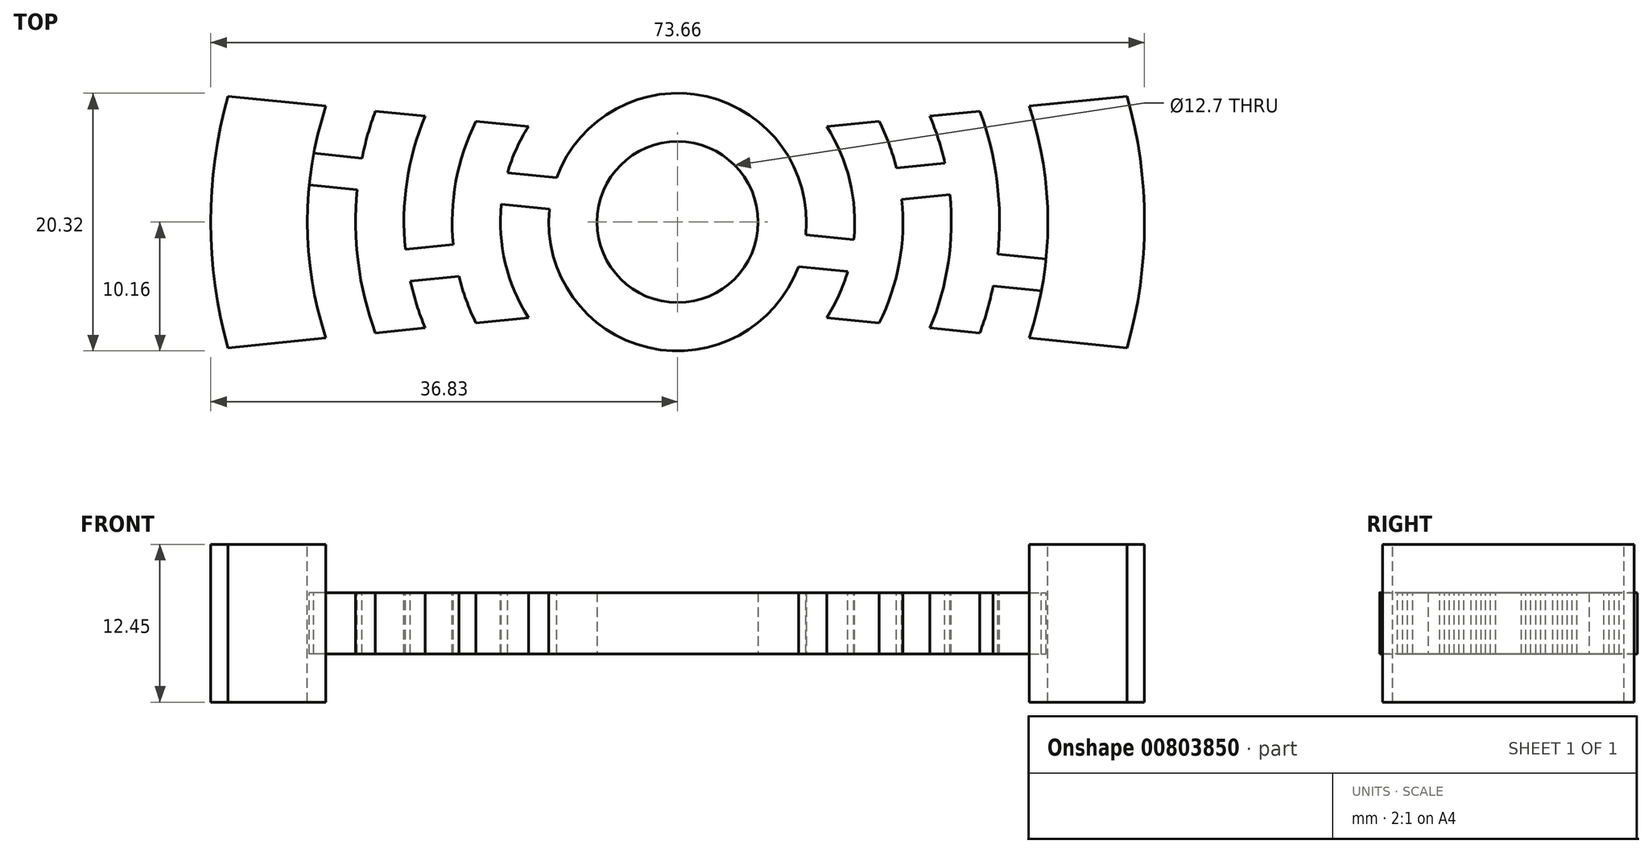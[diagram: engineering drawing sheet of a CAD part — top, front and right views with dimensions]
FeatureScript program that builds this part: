
annotation { "Feature Type Name" : "Feature", "Feature Type Description" : "" }
export const myFeature = defineFeature(function(context is Context, id is Id, definition is map)
    precondition{}
    {
        {
            var Q0;
            Q0=qCreatedBy(makeId("Top.planeOp"),FACE);
            var sketch = newSketch(context, id + "F0", { "sketchPlane" : qUnion([Q0])});
            skCircle(sketch, "E0", {"center": v(0, 0) * mm, "radius": 6.35 * mm});
            skCircle(sketch, "E1", {"center": v(0, 0) * mm, "radius": 10.16 * mm});
            skLineSegment(sketch, "E2", {"start": v(0, 6.35) * mm, "end": v(-37.9, 10.16) * mm});
            skLineSegment(sketch, "E3", {"start": v(0, -6.35) * mm, "end": v(-37.9, -10.16) * mm});
            skLineSegment(sketch, "E4", {"start": v(0, 6.35) * mm, "end": v(37.9, 10.16) * mm});
            skLineSegment(sketch, "E5", {"start": v(0, -6.35) * mm, "end": v(37.9, -10.16) * mm});
            skLineSegment(sketch, "E6", {"start": v(0, 0) * mm, "end": v(40.64, 0) * mm});
            skLineSegment(sketch, "E7", {"start": v(0, 0) * mm, "end": v(-40.64, 0) * mm});
            skCircle(sketch, "E8", {"center": v(0, 0) * mm, "radius": 39.25 * mm});
            skSolve(sketch);
        }
        {
            var Q0;
            {var subQ0=sQuery(id+"F0.wireOp",EDGE,"E4");var subQ1=sQuery(id+"F0.wireOp",EDGE,"E1");var subQ2=makeQuery(id+"F0.imprint","INTERSECT",VERTEX,{"derivedFrom":[subQ1,subQ0]});Q0=makeQuery(id+"F0.imprint","IMPRINT",FACE,{"disambiguationData":[TD([[makeQuery(id+"F0.imprint","IMPRINT",EDGE,{"disambiguationData":[TD([[subQ2,1.0]])],"derivedFrom":subQ1}),-1.0]])]});}
            var Q1;
            {var subQ0=sQuery(id+"F0.wireOp",EDGE,"E2");var subQ1=sQuery(id+"F0.wireOp",EDGE,"E1");var subQ2=makeQuery(id+"F0.imprint","INTERSECT",VERTEX,{"derivedFrom":[subQ1,subQ0]});Q1=makeQuery(id+"F0.imprint","IMPRINT",FACE,{"disambiguationData":[TD([[makeQuery(id+"F0.imprint","IMPRINT",EDGE,{"disambiguationData":[TD([[subQ2,-1.0]])],"derivedFrom":subQ1}),-1.0]])]});}
            var Q2;
            {var subQ0=sQuery(id+"F0.wireOp",EDGE,"E7");var subQ1=sQuery(id+"F0.wireOp",EDGE,"E1");var subQ2=makeQuery(id+"F0.imprint","INTERSECT",VERTEX,{"derivedFrom":[subQ1,subQ0]});Q2=makeQuery(id+"F0.imprint","IMPRINT",FACE,{"disambiguationData":[TD([[makeQuery(id+"F0.imprint","IMPRINT",EDGE,{"disambiguationData":[TD([[subQ2,-1.0]])],"derivedFrom":subQ1}),-1.0]])]});}
            var Q3;
            {var subQ0=sQuery(id+"F0.wireOp",EDGE,"E6");var subQ1=sQuery(id+"F0.wireOp",EDGE,"E1");var subQ2=makeQuery(id+"F0.imprint","INTERSECT",VERTEX,{"derivedFrom":[subQ1,subQ0]});Q3=makeQuery(id+"F0.imprint","IMPRINT",FACE,{"disambiguationData":[TD([[makeQuery(id+"F0.imprint","IMPRINT",EDGE,{"disambiguationData":[TD([[subQ2,1.0]])],"derivedFrom":subQ1}),-1.0]])]});}
            var Q4;
            {var subQ0=sQuery(id+"F0.wireOp",EDGE,"E2");var subQ5=sQuery(id+"F0.wireOp",EDGE,"E1");var subQ6=makeQuery(id+"F0.imprint","INTERSECT",VERTEX,{"derivedFrom":[subQ5,subQ0]});Q4=makeQuery(id+"F0.imprint","IMPRINT",FACE,{"disambiguationData":[TD([[makeQuery(id+"F0.imprint","IMPRINT",EDGE,{"disambiguationData":[TD([[subQ6,-1.0]])],"derivedFrom":subQ5}),1.0]])]});}
            var Q5;
            {var subQ3=sQuery(id+"F0.wireOp",EDGE,"E7");var subQ5=sQuery(id+"F0.wireOp",EDGE,"E1");var subQ6=makeQuery(id+"F0.imprint","INTERSECT",VERTEX,{"derivedFrom":[subQ5,subQ3]});Q5=makeQuery(id+"F0.imprint","IMPRINT",FACE,{"disambiguationData":[TD([[makeQuery(id+"F0.imprint","IMPRINT",EDGE,{"disambiguationData":[TD([[subQ6,-1.0]])],"derivedFrom":subQ5}),1.0]])]});}
            var Q6;
            {var subQ3=sQuery(id+"F0.wireOp",EDGE,"E6");var subQ5=sQuery(id+"F0.wireOp",EDGE,"E1");var subQ6=makeQuery(id+"F0.imprint","INTERSECT",VERTEX,{"derivedFrom":[subQ5,subQ3]});Q6=makeQuery(id+"F0.imprint","IMPRINT",FACE,{"disambiguationData":[TD([[makeQuery(id+"F0.imprint","IMPRINT",EDGE,{"disambiguationData":[TD([[subQ6,1.0]])],"derivedFrom":subQ5}),1.0]])]});}
            var Q7;
            {var subQ0=sQuery(id+"F0.wireOp",EDGE,"E4");var subQ5=sQuery(id+"F0.wireOp",EDGE,"E1");var subQ6=makeQuery(id+"F0.imprint","INTERSECT",VERTEX,{"derivedFrom":[subQ5,subQ0]});Q7=makeQuery(id+"F0.imprint","IMPRINT",FACE,{"disambiguationData":[TD([[makeQuery(id+"F0.imprint","IMPRINT",EDGE,{"disambiguationData":[TD([[subQ6,1.0]])],"derivedFrom":subQ5}),1.0]])]});}
            var Q8;
            {var subQ0=sQuery(id+"F0.wireOp",EDGE,"E4");var subQ1=sQuery(id+"F0.wireOp",EDGE,"E1");var subQ2=makeQuery(id+"F0.imprint","INTERSECT",VERTEX,{"derivedFrom":[subQ1,subQ0]});Q8=makeQuery(id+"F0.imprint","IMPRINT",FACE,{"disambiguationData":[TD([[makeQuery(id+"F0.imprint","IMPRINT",EDGE,{"disambiguationData":[TD([[subQ2,-1.0]])],"derivedFrom":subQ1}),1.0]])]});}
            var Q9;
            {var subQ0=sQuery(id+"F0.wireOp",EDGE,"E3");var subQ1=sQuery(id+"F0.wireOp",EDGE,"E1");var subQ2=makeQuery(id+"F0.imprint","INTERSECT",VERTEX,{"derivedFrom":[subQ1,subQ0]});Q9=makeQuery(id+"F0.imprint","IMPRINT",FACE,{"disambiguationData":[TD([[makeQuery(id+"F0.imprint","IMPRINT",EDGE,{"disambiguationData":[TD([[subQ2,-1.0]])],"derivedFrom":subQ1}),1.0]])]});}
            extrude(context, id + "F1", {"entities" : qUnion([Q0, Q1, Q2, Q3, Q4, Q5, Q6, Q7, Q8, Q9]), "depth" : 4.83 * mm, "offsetDistance" : 25.4 * mm});
        }
        {
            var Q0;
            Q0=makeQuery(id+"F1.opExtrude","CAP_FACE",FACE,{"disambiguationData":[OSD([sQuery(id+"F0.wireOp",EDGE,"E0"),sQuery(id+"F0.wireOp",EDGE,"E1"),sQuery(id+"F0.wireOp",EDGE,"E2"),sQuery(id+"F0.wireOp",EDGE,"E3"),sQuery(id+"F0.wireOp",EDGE,"E4"),sQuery(id+"F0.wireOp",EDGE,"E5"),sQuery(id+"F0.wireOp",EDGE,"liuHo2mv-Kwf8-5aol-AB9t-589r57ZSycez"),sQuery(id+"F0.wireOp",EDGE,"nakFOlJR-s7SA-ednX-MnhK-JYGa1BLhNWg9")])],"isStart":false});
            var sketch = newSketch(context, id + "F2", { "sketchPlane" : qUnion([Q0])});
            skCircle(sketch, "E9", {"center": v(0, 0) * mm, "radius": 6.35 * mm});
            skCircle(sketch, "E10", {"center": v(0, 0) * mm, "radius": 10.16 * mm});
            skCircle(sketch, "E11", {"center": v(0, 0) * mm, "radius": 39.25 * mm});
            skCircle(sketch, "E12", {"center": v(0, 0) * mm, "radius": 33.02 * mm});
            skCircle(sketch, "E13", {"center": v(0, 0) * mm, "radius": 25.4 * mm});
            skCircle(sketch, "E14", {"center": v(0, 0) * mm, "radius": 21.59 * mm});
            skCircle(sketch, "E15", {"center": v(0, 0) * mm, "radius": 29.21 * mm});
            skCircle(sketch, "E16", {"center": v(0, 0) * mm, "radius": 13.97 * mm});
            skCircle(sketch, "E17", {"center": v(0, 0) * mm, "radius": 17.78 * mm});
            skCircle(sketch, "E18", {"center": v(0, 0) * mm, "radius": 2.54 * mm});
            skLineSegment(sketch, "E19", {"start": v(0, -2.54) * mm, "end": v(-38.72, -6.43) * mm});
            skLineSegment(sketch, "E20", {"start": v(0, 2.54) * mm, "end": v(-38.72, 6.43) * mm});
            skLineSegment(sketch, "E21", {"start": v(0, -2.54) * mm, "end": v(38.72, -6.43) * mm});
            skLineSegment(sketch, "E22", {"start": v(0, 2.54) * mm, "end": v(38.72, 6.43) * mm});
            skLineSegment(sketch, "E23", {"start": v(0, 0) * mm, "end": v(-39.05, 3.92) * mm});
            skLineSegment(sketch, "E24", {"start": v(0, 0) * mm, "end": v(39.05, 3.92) * mm});
            skLineSegment(sketch, "E25", {"start": v(0, 0) * mm, "end": v(39.05, -3.92) * mm});
            skLineSegment(sketch, "E26", {"start": v(0, 0) * mm, "end": v(-39.05, -3.92) * mm});
            skCircle(sketch, "E27", {"center": v(0, 0) * mm, "radius": 36.83 * mm});
            skCircle(sketch, "E28", {"center": v(0.53, -0.92) * mm, "radius": 41.7 * mm});
            skSolve(sketch);
        }
        {
            var Q0;
            {var subQ0=sQuery(id+"F2.wireOp",EDGE,"E20");var subQ1=sQuery(id+"F2.wireOp",EDGE,"E14");var subQ2=makeQuery(id+"F2.imprint","INTERSECT",VERTEX,{"derivedFrom":[subQ1,subQ0]});Q0=makeQuery(id+"F2.imprint","IMPRINT",FACE,{"disambiguationData":[TD([[makeQuery(id+"F2.imprint","IMPRINT",EDGE,{"disambiguationData":[TD([[subQ2,1.0]])],"derivedFrom":subQ1}),1.0]])]});}
            var Q1;
            {var subQ0=sQuery(id+"F2.wireOp",EDGE,"E20");var subQ1=sQuery(id+"F2.wireOp",EDGE,"E14");var subQ2=makeQuery(id+"F2.imprint","INTERSECT",VERTEX,{"derivedFrom":[subQ1,subQ0]});Q1=makeQuery(id+"F2.imprint","IMPRINT",FACE,{"disambiguationData":[TD([[makeQuery(id+"F2.imprint","IMPRINT",EDGE,{"disambiguationData":[TD([[subQ2,-1.0]])],"derivedFrom":subQ1}),1.0]])]});}
            var Q2;
            {var subQ0=sQuery(id+"F2.wireOp",EDGE,"E21");var subQ1=sQuery(id+"F2.wireOp",EDGE,"E14");var subQ2=makeQuery(id+"F2.imprint","INTERSECT",VERTEX,{"derivedFrom":[subQ1,subQ0]});Q2=makeQuery(id+"F2.imprint","IMPRINT",FACE,{"disambiguationData":[TD([[makeQuery(id+"F2.imprint","IMPRINT",EDGE,{"disambiguationData":[TD([[subQ2,1.0]])],"derivedFrom":subQ1}),1.0]])]});}
            var Q3;
            {var subQ0=sQuery(id+"F2.wireOp",EDGE,"E19");var subQ1=sQuery(id+"F2.wireOp",EDGE,"E14");var subQ2=makeQuery(id+"F2.imprint","INTERSECT",VERTEX,{"derivedFrom":[subQ1,subQ0]});Q3=makeQuery(id+"F2.imprint","IMPRINT",FACE,{"disambiguationData":[TD([[makeQuery(id+"F2.imprint","IMPRINT",EDGE,{"disambiguationData":[TD([[subQ2,-1.0]])],"derivedFrom":subQ1}),1.0]])]});}
            var Q4;
            {var subQ0=sQuery(id+"F2.wireOp",EDGE,"E19");var subQ1=sQuery(id+"F2.wireOp",EDGE,"E13");var subQ2=makeQuery(id+"F2.imprint","INTERSECT",VERTEX,{"derivedFrom":[subQ1,subQ0]});Q4=makeQuery(id+"F2.imprint","IMPRINT",FACE,{"disambiguationData":[TD([[makeQuery(id+"F2.imprint","IMPRINT",EDGE,{"disambiguationData":[TD([[subQ2,-1.0]])],"derivedFrom":subQ1}),-1.0]])]});}
            var Q5;
            {var subQ0=sQuery(id+"F2.wireOp",EDGE,"E23");var subQ1=sQuery(id+"F2.wireOp",EDGE,"E13");var subQ2=makeQuery(id+"F2.imprint","INTERSECT",VERTEX,{"derivedFrom":[subQ1,subQ0]});Q5=makeQuery(id+"F2.imprint","IMPRINT",FACE,{"disambiguationData":[TD([[makeQuery(id+"F2.imprint","IMPRINT",EDGE,{"disambiguationData":[TD([[subQ2,-1.0]])],"derivedFrom":subQ1}),-1.0]])]});}
            var Q6;
            {var subQ0=sQuery(id+"F2.wireOp",EDGE,"E20");var subQ1=sQuery(id+"F2.wireOp",EDGE,"E13");var subQ2=makeQuery(id+"F2.imprint","INTERSECT",VERTEX,{"derivedFrom":[subQ1,subQ0]});Q6=makeQuery(id+"F2.imprint","IMPRINT",FACE,{"disambiguationData":[TD([[makeQuery(id+"F2.imprint","IMPRINT",EDGE,{"disambiguationData":[TD([[subQ2,1.0]])],"derivedFrom":subQ1}),-1.0]])]});}
            var Q7;
            {var subQ0=sQuery(id+"F2.wireOp",EDGE,"E24");var subQ1=sQuery(id+"F2.wireOp",EDGE,"E14");var subQ2=makeQuery(id+"F2.imprint","INTERSECT",VERTEX,{"derivedFrom":[subQ1,subQ0]});Q7=makeQuery(id+"F2.imprint","IMPRINT",FACE,{"disambiguationData":[TD([[makeQuery(id+"F2.imprint","IMPRINT",EDGE,{"disambiguationData":[TD([[subQ2,1.0]])],"derivedFrom":subQ1}),1.0]])]});}
            var Q8;
            {var subQ0=sQuery(id+"F2.wireOp",EDGE,"E21");var subQ1=sQuery(id+"F2.wireOp",EDGE,"E14");var subQ2=makeQuery(id+"F2.imprint","INTERSECT",VERTEX,{"derivedFrom":[subQ1,subQ0]});Q8=makeQuery(id+"F2.imprint","IMPRINT",FACE,{"disambiguationData":[TD([[makeQuery(id+"F2.imprint","IMPRINT",EDGE,{"disambiguationData":[TD([[subQ2,-1.0]])],"derivedFrom":subQ1}),1.0]])]});}
            var Q9;
            {var subQ0=sQuery(id+"F2.wireOp",EDGE,"E22");var subQ1=sQuery(id+"F2.wireOp",EDGE,"E14");var subQ2=makeQuery(id+"F2.imprint","INTERSECT",VERTEX,{"derivedFrom":[subQ1,subQ0]});Q9=makeQuery(id+"F2.imprint","IMPRINT",FACE,{"disambiguationData":[TD([[makeQuery(id+"F2.imprint","IMPRINT",EDGE,{"disambiguationData":[TD([[subQ2,-1.0]])],"derivedFrom":subQ1}),1.0]])]});}
            var Q10;
            {var subQ0=sQuery(id+"F2.wireOp",EDGE,"E22");var subQ1=sQuery(id+"F2.wireOp",EDGE,"E13");var subQ2=makeQuery(id+"F2.imprint","INTERSECT",VERTEX,{"derivedFrom":[subQ1,subQ0]});Q10=makeQuery(id+"F2.imprint","IMPRINT",FACE,{"disambiguationData":[TD([[makeQuery(id+"F2.imprint","IMPRINT",EDGE,{"disambiguationData":[TD([[subQ2,-1.0]])],"derivedFrom":subQ1}),-1.0]])]});}
            var Q11;
            {var subQ0=sQuery(id+"F2.wireOp",EDGE,"E22");var subQ1=sQuery(id+"F2.wireOp",EDGE,"E13");var subQ2=makeQuery(id+"F2.imprint","INTERSECT",VERTEX,{"derivedFrom":[subQ1,subQ0]});Q11=makeQuery(id+"F2.imprint","IMPRINT",FACE,{"disambiguationData":[TD([[makeQuery(id+"F2.imprint","IMPRINT",EDGE,{"disambiguationData":[TD([[subQ2,1.0]])],"derivedFrom":subQ1}),-1.0]])]});}
            var Q12;
            {var subQ0=sQuery(id+"F2.wireOp",EDGE,"E24");var subQ1=sQuery(id+"F2.wireOp",EDGE,"E13");var subQ2=makeQuery(id+"F2.imprint","INTERSECT",VERTEX,{"derivedFrom":[subQ1,subQ0]});Q12=makeQuery(id+"F2.imprint","IMPRINT",FACE,{"disambiguationData":[TD([[makeQuery(id+"F2.imprint","IMPRINT",EDGE,{"disambiguationData":[TD([[subQ2,1.0]])],"derivedFrom":subQ1}),-1.0]])]});}
            var Q13;
            {var subQ0=sQuery(id+"F2.wireOp",EDGE,"E21");var subQ1=sQuery(id+"F2.wireOp",EDGE,"E13");var subQ2=makeQuery(id+"F2.imprint","INTERSECT",VERTEX,{"derivedFrom":[subQ1,subQ0]});Q13=makeQuery(id+"F2.imprint","IMPRINT",FACE,{"disambiguationData":[TD([[makeQuery(id+"F2.imprint","IMPRINT",EDGE,{"disambiguationData":[TD([[subQ2,1.0]])],"derivedFrom":subQ1}),-1.0]])]});}
            var Q14;
            {var subQ0=sQuery(id+"F2.wireOp",EDGE,"E23");var subQ1=sQuery(id+"F2.wireOp",EDGE,"E14");var subQ2=makeQuery(id+"F2.imprint","INTERSECT",VERTEX,{"derivedFrom":[subQ1,subQ0]});Q14=makeQuery(id+"F2.imprint","IMPRINT",FACE,{"disambiguationData":[TD([[makeQuery(id+"F2.imprint","IMPRINT",EDGE,{"disambiguationData":[TD([[subQ2,-1.0]])],"derivedFrom":subQ1}),1.0]])]});}
            var Q15;
            {var subQ0=sQuery(id+"F2.wireOp",EDGE,"E26");var subQ1=sQuery(id+"F2.wireOp",EDGE,"E13");var subQ2=makeQuery(id+"F2.imprint","INTERSECT",VERTEX,{"derivedFrom":[subQ1,subQ0]});Q15=makeQuery(id+"F2.imprint","IMPRINT",FACE,{"disambiguationData":[TD([[makeQuery(id+"F2.imprint","IMPRINT",EDGE,{"disambiguationData":[TD([[subQ2,-1.0]])],"derivedFrom":subQ1}),-1.0]])]});}
            var Q16;
            {var subQ0=sQuery(id+"F2.wireOp",EDGE,"E19");var subQ1=sQuery(id+"F2.wireOp",EDGE,"E11");var subQ2=makeQuery(id+"F2.imprint","INTERSECT",VERTEX,{"derivedFrom":[subQ1,subQ0]});Q16=makeQuery(id+"F2.imprint","IMPRINT",FACE,{"disambiguationData":[TD([[makeQuery(id+"F2.imprint","IMPRINT",EDGE,{"disambiguationData":[TD([[subQ2,1.0]])],"derivedFrom":subQ1}),1.0]])]});}
            var Q17;
            {var subQ0=sQuery(id+"F2.wireOp",EDGE,"E11");var subQ1=makeQuery(id+"F1.opExtrude","CAP_EDGE",EDGE,{"disambiguationData":[OSD([sQuery(id+"F0.wireOp",EDGE,"E3")])],"isStart":false});var subQ2=makeQuery(id+"F2.imprint","INTERSECT",VERTEX,{"derivedFrom":[subQ1,subQ0]});Q17=makeQuery(id+"F2.imprint","IMPRINT",FACE,{"disambiguationData":[TD([[makeQuery(id+"F2.imprint","IMPRINT",EDGE,{"disambiguationData":[TD([[subQ2,1.0]])],"derivedFrom":subQ0}),1.0]])]});}
            var Q18;
            {var subQ0=sQuery(id+"F2.wireOp",EDGE,"E23");var subQ1=sQuery(id+"F2.wireOp",EDGE,"E11");var subQ2=makeQuery(id+"F2.imprint","INTERSECT",VERTEX,{"derivedFrom":[subQ1,subQ0]});Q18=makeQuery(id+"F2.imprint","IMPRINT",FACE,{"disambiguationData":[TD([[makeQuery(id+"F2.imprint","IMPRINT",EDGE,{"disambiguationData":[TD([[subQ2,-1.0]])],"derivedFrom":subQ1}),1.0]])]});}
            var Q19;
            {var subQ0=sQuery(id+"F2.wireOp",EDGE,"E20");var subQ1=sQuery(id+"F2.wireOp",EDGE,"E11");var subQ2=makeQuery(id+"F2.imprint","INTERSECT",VERTEX,{"derivedFrom":[subQ1,subQ0]});Q19=makeQuery(id+"F2.imprint","IMPRINT",FACE,{"disambiguationData":[TD([[makeQuery(id+"F2.imprint","IMPRINT",EDGE,{"disambiguationData":[TD([[subQ2,-1.0]])],"derivedFrom":subQ1}),1.0]])]});}
            var Q20;
            {var subQ0=sQuery(id+"F2.wireOp",EDGE,"E11");var subQ1=makeQuery(id+"F1.opExtrude","CAP_EDGE",EDGE,{"disambiguationData":[OSD([sQuery(id+"F0.wireOp",EDGE,"E2")])],"isStart":false});var subQ2=makeQuery(id+"F2.imprint","INTERSECT",VERTEX,{"derivedFrom":[subQ1,subQ0]});Q20=makeQuery(id+"F2.imprint","IMPRINT",FACE,{"disambiguationData":[TD([[makeQuery(id+"F2.imprint","IMPRINT",EDGE,{"disambiguationData":[TD([[subQ2,-1.0]])],"derivedFrom":subQ0}),1.0]])]});}
            var Q21;
            {var subQ0=sQuery(id+"F2.wireOp",EDGE,"E11");var subQ1=makeQuery(id+"F1.opExtrude","CAP_EDGE",EDGE,{"disambiguationData":[OSD([sQuery(id+"F0.wireOp",EDGE,"E4")])],"isStart":false});var subQ2=makeQuery(id+"F2.imprint","INTERSECT",VERTEX,{"derivedFrom":[subQ1,subQ0]});Q21=makeQuery(id+"F2.imprint","IMPRINT",FACE,{"disambiguationData":[TD([[makeQuery(id+"F2.imprint","IMPRINT",EDGE,{"disambiguationData":[TD([[subQ2,1.0]])],"derivedFrom":subQ0}),1.0]])]});}
            var Q22;
            {var subQ0=sQuery(id+"F2.wireOp",EDGE,"E22");var subQ1=sQuery(id+"F2.wireOp",EDGE,"E11");var subQ2=makeQuery(id+"F2.imprint","INTERSECT",VERTEX,{"derivedFrom":[subQ1,subQ0]});Q22=makeQuery(id+"F2.imprint","IMPRINT",FACE,{"disambiguationData":[TD([[makeQuery(id+"F2.imprint","IMPRINT",EDGE,{"disambiguationData":[TD([[subQ2,1.0]])],"derivedFrom":subQ1}),1.0]])]});}
            var Q23;
            {var subQ0=sQuery(id+"F2.wireOp",EDGE,"E24");var subQ1=sQuery(id+"F2.wireOp",EDGE,"E11");var subQ2=makeQuery(id+"F2.imprint","INTERSECT",VERTEX,{"derivedFrom":[subQ1,subQ0]});Q23=makeQuery(id+"F2.imprint","IMPRINT",FACE,{"disambiguationData":[TD([[makeQuery(id+"F2.imprint","IMPRINT",EDGE,{"disambiguationData":[TD([[subQ2,1.0]])],"derivedFrom":subQ1}),1.0]])]});}
            var Q24;
            {var subQ0=sQuery(id+"F2.wireOp",EDGE,"E21");var subQ1=sQuery(id+"F2.wireOp",EDGE,"E11");var subQ2=makeQuery(id+"F2.imprint","INTERSECT",VERTEX,{"derivedFrom":[subQ1,subQ0]});Q24=makeQuery(id+"F2.imprint","IMPRINT",FACE,{"disambiguationData":[TD([[makeQuery(id+"F2.imprint","IMPRINT",EDGE,{"disambiguationData":[TD([[subQ2,-1.0]])],"derivedFrom":subQ1}),1.0]])]});}
            var Q25;
            {var subQ0=sQuery(id+"F2.wireOp",EDGE,"E11");var subQ1=makeQuery(id+"F1.opExtrude","CAP_EDGE",EDGE,{"disambiguationData":[OSD([sQuery(id+"F0.wireOp",EDGE,"E5")])],"isStart":false});var subQ2=makeQuery(id+"F2.imprint","INTERSECT",VERTEX,{"derivedFrom":[subQ1,subQ0]});Q25=makeQuery(id+"F2.imprint","IMPRINT",FACE,{"disambiguationData":[TD([[makeQuery(id+"F2.imprint","IMPRINT",EDGE,{"disambiguationData":[TD([[subQ2,-1.0]])],"derivedFrom":subQ0}),1.0]])]});}
            var Q26;
            {var subQ0=sQuery(id+"F2.wireOp",EDGE,"E10");var subQ1=makeQuery(id+"F1.opExtrude","CAP_EDGE",EDGE,{"disambiguationData":[OSD([sQuery(id+"F0.wireOp",EDGE,"E5")])],"isStart":false});var subQ2=makeQuery(id+"F2.imprint","INTERSECT",VERTEX,{"derivedFrom":[subQ1,subQ0]});Q26=makeQuery(id+"F2.imprint","IMPRINT",FACE,{"disambiguationData":[TD([[makeQuery(id+"F2.imprint","IMPRINT",EDGE,{"disambiguationData":[TD([[subQ2,-1.0]])],"derivedFrom":subQ0}),-1.0]])]});}
            var Q27;
            {var subQ0=sQuery(id+"F2.wireOp",EDGE,"E24");var subQ1=sQuery(id+"F2.wireOp",EDGE,"E10");var subQ2=makeQuery(id+"F2.imprint","INTERSECT",VERTEX,{"derivedFrom":[subQ1,subQ0]});Q27=makeQuery(id+"F2.imprint","IMPRINT",FACE,{"disambiguationData":[TD([[makeQuery(id+"F2.imprint","IMPRINT",EDGE,{"disambiguationData":[TD([[subQ2,1.0]])],"derivedFrom":subQ1}),-1.0]])]});}
            var Q28;
            {var subQ0=sQuery(id+"F2.wireOp",EDGE,"E22");var subQ1=sQuery(id+"F2.wireOp",EDGE,"E10");var subQ2=makeQuery(id+"F2.imprint","INTERSECT",VERTEX,{"derivedFrom":[subQ1,subQ0]});Q28=makeQuery(id+"F2.imprint","IMPRINT",FACE,{"disambiguationData":[TD([[makeQuery(id+"F2.imprint","IMPRINT",EDGE,{"disambiguationData":[TD([[subQ2,1.0]])],"derivedFrom":subQ1}),-1.0]])]});}
            var Q29;
            {var subQ0=sQuery(id+"F2.wireOp",EDGE,"E10");var subQ1=makeQuery(id+"F1.opExtrude","CAP_EDGE",EDGE,{"disambiguationData":[OSD([sQuery(id+"F0.wireOp",EDGE,"E4")])],"isStart":false});var subQ2=makeQuery(id+"F2.imprint","INTERSECT",VERTEX,{"derivedFrom":[subQ1,subQ0]});Q29=makeQuery(id+"F2.imprint","IMPRINT",FACE,{"disambiguationData":[TD([[makeQuery(id+"F2.imprint","IMPRINT",EDGE,{"disambiguationData":[TD([[subQ2,1.0]])],"derivedFrom":subQ0}),-1.0]])]});}
            var Q30;
            {var subQ0=sQuery(id+"F2.wireOp",EDGE,"E10");var subQ1=makeQuery(id+"F1.opExtrude","CAP_EDGE",EDGE,{"disambiguationData":[OSD([sQuery(id+"F0.wireOp",EDGE,"E2")])],"isStart":false});var subQ2=makeQuery(id+"F2.imprint","INTERSECT",VERTEX,{"derivedFrom":[subQ1,subQ0]});Q30=makeQuery(id+"F2.imprint","IMPRINT",FACE,{"disambiguationData":[TD([[makeQuery(id+"F2.imprint","IMPRINT",EDGE,{"disambiguationData":[TD([[subQ2,-1.0]])],"derivedFrom":subQ0}),-1.0]])]});}
            var Q31;
            {var subQ0=sQuery(id+"F2.wireOp",EDGE,"E23");var subQ1=sQuery(id+"F2.wireOp",EDGE,"E10");var subQ2=makeQuery(id+"F2.imprint","INTERSECT",VERTEX,{"derivedFrom":[subQ1,subQ0]});Q31=makeQuery(id+"F2.imprint","IMPRINT",FACE,{"disambiguationData":[TD([[makeQuery(id+"F2.imprint","IMPRINT",EDGE,{"disambiguationData":[TD([[subQ2,-1.0]])],"derivedFrom":subQ1}),-1.0]])]});}
            var Q32;
            {var subQ0=sQuery(id+"F2.wireOp",EDGE,"E26");var subQ1=sQuery(id+"F2.wireOp",EDGE,"E10");var subQ2=makeQuery(id+"F2.imprint","INTERSECT",VERTEX,{"derivedFrom":[subQ1,subQ0]});Q32=makeQuery(id+"F2.imprint","IMPRINT",FACE,{"disambiguationData":[TD([[makeQuery(id+"F2.imprint","IMPRINT",EDGE,{"disambiguationData":[TD([[subQ2,-1.0]])],"derivedFrom":subQ1}),-1.0]])]});}
            var Q33;
            {var subQ0=sQuery(id+"F2.wireOp",EDGE,"E10");var subQ1=makeQuery(id+"F1.opExtrude","CAP_EDGE",EDGE,{"disambiguationData":[OSD([sQuery(id+"F0.wireOp",EDGE,"E3")])],"isStart":false});var subQ2=makeQuery(id+"F2.imprint","INTERSECT",VERTEX,{"derivedFrom":[subQ1,subQ0]});Q33=makeQuery(id+"F2.imprint","IMPRINT",FACE,{"disambiguationData":[TD([[makeQuery(id+"F2.imprint","IMPRINT",EDGE,{"disambiguationData":[TD([[subQ2,1.0]])],"derivedFrom":subQ0}),-1.0]])]});}
            extrude(context, id + "F3", {"entities" : qUnion([Q0, Q1, Q2, Q3, Q4, Q5, Q6, Q7, Q8, Q9, Q10, Q11, Q12, Q13, Q14, Q15, Q16, Q17, Q18, Q19, Q20, Q21, Q22, Q23, Q24, Q25, Q26, Q27, Q28, Q29, Q30, Q31, Q32, Q33]), "operationType" : NewBodyOperationType.REMOVE, "oppositeDirection" : true, "depth" : 25.4 * mm, "offsetDistance" : 25.4 * mm});
        }
        {
            var Q0;
            Q0=makeQuery(id+"F1.opExtrude","CAP_FACE",FACE,{"disambiguationData":[OSD([sQuery(id+"F0.wireOp",EDGE,"E0"),sQuery(id+"F0.wireOp",EDGE,"E1"),sQuery(id+"F0.wireOp",EDGE,"E2"),sQuery(id+"F0.wireOp",EDGE,"E3"),sQuery(id+"F0.wireOp",EDGE,"E4"),sQuery(id+"F0.wireOp",EDGE,"E5"),sQuery(id+"F0.wireOp",EDGE,"E8")])],"isStart":false});
            var sketch = newSketch(context, id + "F4", { "sketchPlane" : qUnion([Q0])});
            skPoint(sketch, "E29", {"position": v(-36.83, 0) * mm});
            skPoint(sketch, "E30", {"position": v(36.83, 0) * mm});
            skLineSegment(sketch, "E31", {"start": v(-35.47, 9.91) * mm, "end": v(-27.74, 9.14) * mm});
            skLineSegment(sketch, "E32", {"start": v(-27.74, -9.14) * mm, "end": v(-35.47, -9.91) * mm});
            skLineSegment(sketch, "E33", {"start": v(27.74, 9.14) * mm, "end": v(35.47, 9.91) * mm});
            skLineSegment(sketch, "E34", {"start": v(35.47, -9.91) * mm, "end": v(27.74, -9.14) * mm});
            skArc(sketch, "E35", {"start": v(35.47, -9.91) * mm, "mid": v(36.83, 0) * mm, "end": v(35.47, 9.91) * mm});
            skArc(sketch, "E36", {"start": v(-35.47, 9.91) * mm, "mid": v(-36.83, 0) * mm, "end": v(-35.47, -9.91) * mm});
            skArc(sketch, "E37", {"start": v(-27.74, 9.14) * mm, "mid": v(-29.21, 0) * mm, "end": v(-27.74, -9.14) * mm});
            skArc(sketch, "E38", {"start": v(27.74, -9.14) * mm, "mid": v(29.21, 0) * mm, "end": v(27.74, 9.14) * mm});
            skSolve(sketch);
        }
        {
            var Q0;
            Q0=qSketchRegion(id+"F4",true);
            extrude(context, id + "F5", {"entities" : qUnion([Q0]), "operationType" : NewBodyOperationType.ADD, "depth" : 3.8 * mm, "offsetDistance" : 25.4 * mm, "hasSecondDirection" : true, "secondDirectionOppositeDirection" : true, "secondDirectionDepth" : 8.64 * mm});
        }
    });
